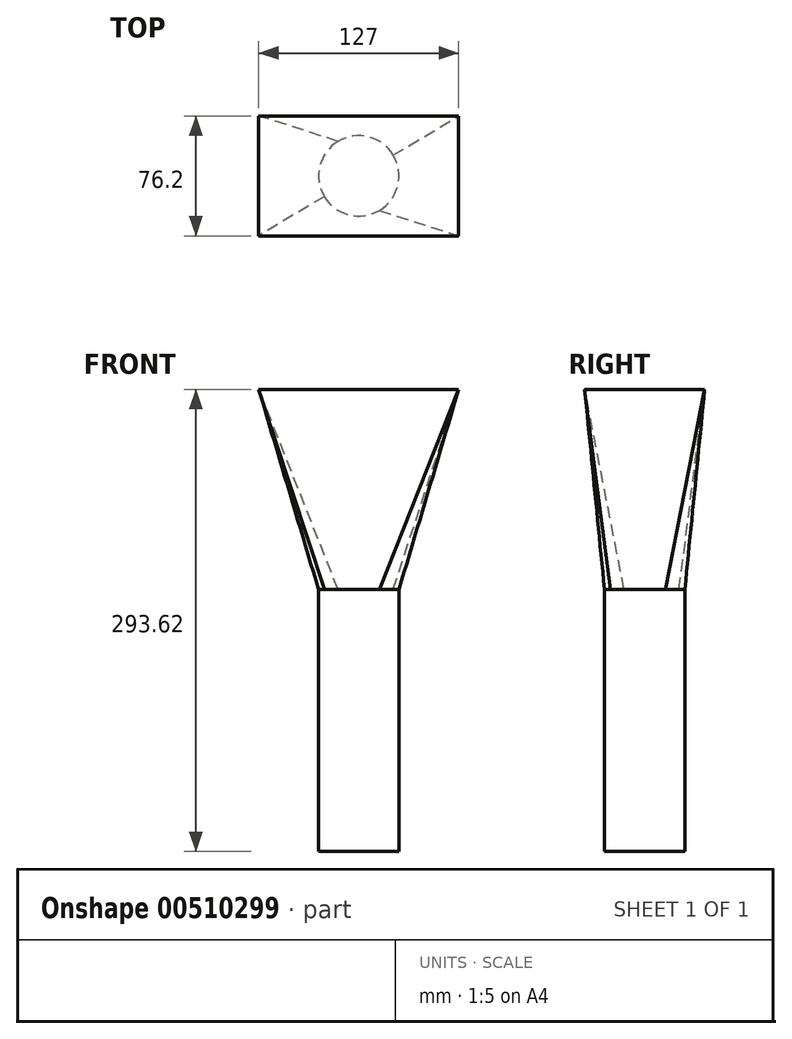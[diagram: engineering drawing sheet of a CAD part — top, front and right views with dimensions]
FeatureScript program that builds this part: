
annotation { "Feature Type Name" : "Feature", "Feature Type Description" : "" }
export const myFeature = defineFeature(function(context is Context, id is Id, definition is map)
    precondition{}
    {
        {
            var Q0;
            Q0=qCreatedBy(makeId("Top.planeOp"),FACE);
            cPlane(context, id + "F0", {"entities" : qUnion([Q0]), "cplaneType" : CPlaneType.OFFSET, "offset" : 127 * mm, "width" : 152.4 * mm, "height" : 152.4 * mm});
        }
        {
            var Q0;
            Q0=qCreatedBy(id+"F0.planeOp",FACE);
            var sketch = newSketch(context, id + "F1", { "sketchPlane" : qUnion([Q0])});
            skLineSegment(sketch, "E0.bottom", {"start": v(63.5, 38.1) * mm, "end": v(-63.5, 38.1) * mm});
            skLineSegment(sketch, "E0.top", {"start": v(63.5, -38.1) * mm, "end": v(-63.5, -38.1) * mm});
            skLineSegment(sketch, "E0.left", {"start": v(63.5, 38.1) * mm, "end": v(63.5, -38.1) * mm});
            skLineSegment(sketch, "E0.right", {"start": v(-63.5, 38.1) * mm, "end": v(-63.5, -38.1) * mm});
            skPoint(sketch, "E0.middle", {"position": v(0, 0) * mm});
            skSolve(sketch);
        }
        {
            var Q0;
            Q0=qCreatedBy(makeId("Top.planeOp"),FACE);
            var sketch = newSketch(context, id + "F2", { "sketchPlane" : qUnion([Q0])});
            skCircle(sketch, "E1", {"center": v(0, 0) * mm, "radius": 25.53 * mm});
            skSolve(sketch);
        }
        {
            var Q0;
            Q0=makeQuery(id+"F2.imprint","IMPRINT",FACE,{"disambiguationData":[TD([[makeQuery(id+"F2.imprint","IMPRINT",EDGE,{"derivedFrom":sQuery(id+"F2.wireOp",EDGE,"E1")}),1.0]])]});
            var Q1;
            Q1=makeQuery(id+"F1.imprint","IMPRINT",FACE,{"disambiguationData":[TD([[makeQuery(id+"F1.imprint","IMPRINT",EDGE,{"derivedFrom":sQuery(id+"F1.wireOp",EDGE,"E0.bottom")}),1.0]])]});
            loft(context, id + "F3", {"sheetProfilesArray" : [{ "sheetProfileEntities" : qUnion([Q0]) }, { "sheetProfileEntities" : qUnion([Q1]) }]});
        }
        {
            var Q0;
            Q0=makeQuery(id+"F3.opLoft","CAP_FACE",FACE,{"disambiguationData":[OSD([makeQuery(id+"F2.imprint","IMPRINT",FACE,{"disambiguationData":[TD([[makeQuery(id+"F2.imprint","IMPRINT",EDGE,{"derivedFrom":sQuery(id+"F2.wireOp",EDGE,"E1")}),1.0]])]})])],"isStart":true});
            extrude(context, id + "F4", {"entities" : qUnion([Q0]), "operationType" : NewBodyOperationType.ADD, "depth" : 166.62 * mm});
        }
    });
